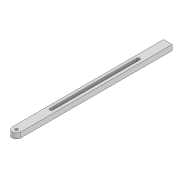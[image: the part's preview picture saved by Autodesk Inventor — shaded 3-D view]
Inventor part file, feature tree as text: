
AUTODESK INVENTOR PART (.ipt)
format: ipt  version: 2022 (Build 260153000, 153)  size: 128,000 bytes
history: native  units: mm
features: extrude x3, sketch x3, projected_geometry x2, fillet x1
ambient origin geometry x8: Origin, YZ Plane, XZ Plane, XY Plane, X Axis, Y Axis, Z Axis, Center Point
bodies: Solid1 (feature_tree)
feature tree (9):
  extrude  "Extrusion1"  Depth=10.0mm
  extrude  "Extrusion2"  Depth=40.0mm
  fillet  "Fillet1"  Radius=140.0mm
  extrude  "Extrusion3"  Depth=6.0mm TaperAngle=0.0deg
  sketch  "Sketch1"  dims[d0=180.0mm d1=10.0mm]
  sketch  "Sketch2"  dims[d2=3.3mm d3=40.0mm d5=140.0mm]
  projected_geometry  "Projected Loop1"
  projected_geometry  "Projected Loop2"
  sketch  "Sketch3"  dims[d6=3.3mm d7=6.0mm d8=0.0mm d9=6.0mm d10=498.004mm d11=90.0mm d12=10.0mm d13=0.0mm d14=2.0mm d15=100.0mm d16=0.0mm]
